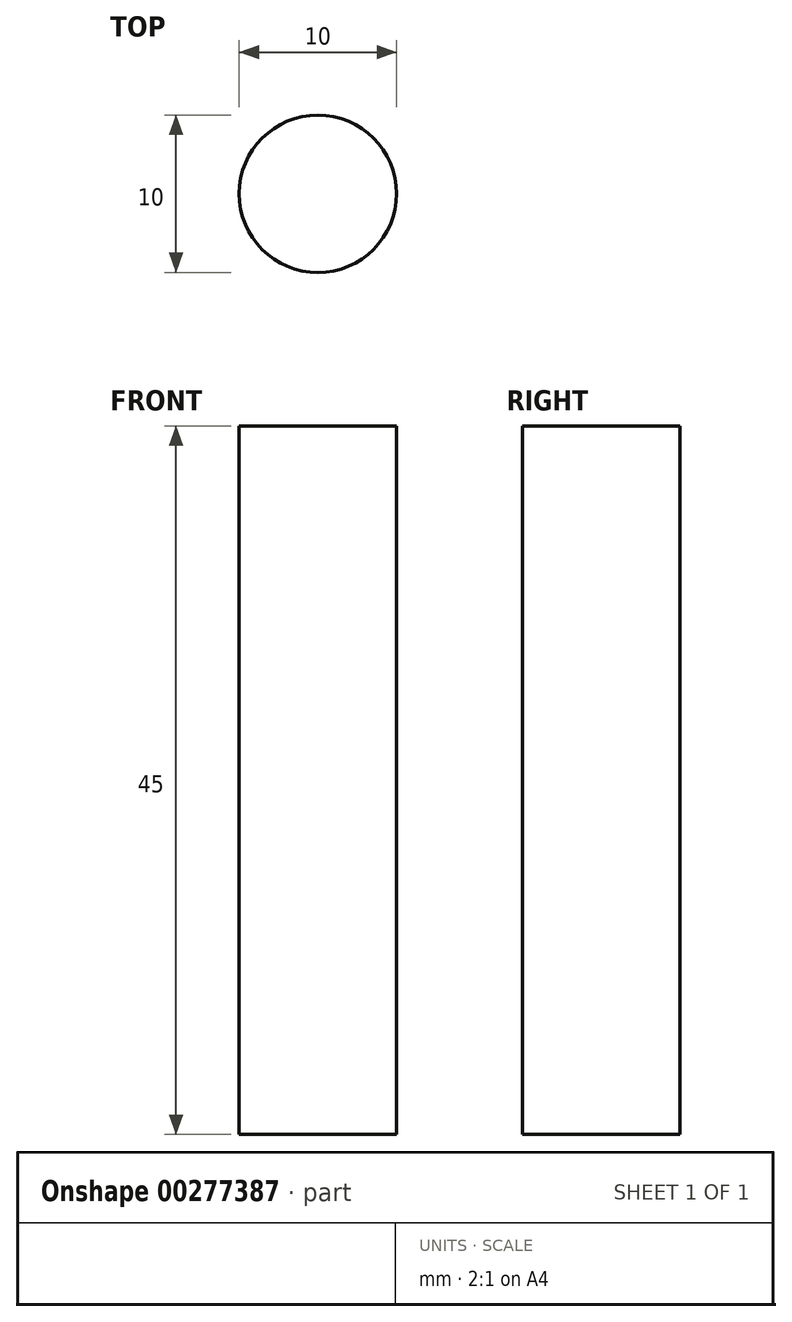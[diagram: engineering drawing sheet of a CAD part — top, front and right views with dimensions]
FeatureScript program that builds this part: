
annotation { "Feature Type Name" : "Feature", "Feature Type Description" : "" }
export const myFeature = defineFeature(function(context is Context, id is Id, definition is map)
    precondition{}
    {
        {
            var Q0;
            Q0=qCreatedBy(makeId("Top.planeOp"),FACE);
            var sketch = newSketch(context, id + "F0", { "sketchPlane" : qUnion([Q0])});
            skCircle(sketch, "E0", {"center": v(0, 0) * mm, "radius": 5 * mm});
            skSolve(sketch);
        }
        {
            var Q0;
            Q0=makeQuery(id+"F0.imprint","IMPRINT",FACE,{"disambiguationData":[TD([[makeQuery(id+"F0.imprint","IMPRINT",EDGE,{"derivedFrom":sQuery(id+"F0.wireOp",EDGE,"E0")}),1.0]])]});
            extrude(context, id + "F1", {"entities" : qUnion([Q0]), "depth" : 45 * mm});
        }
    });
